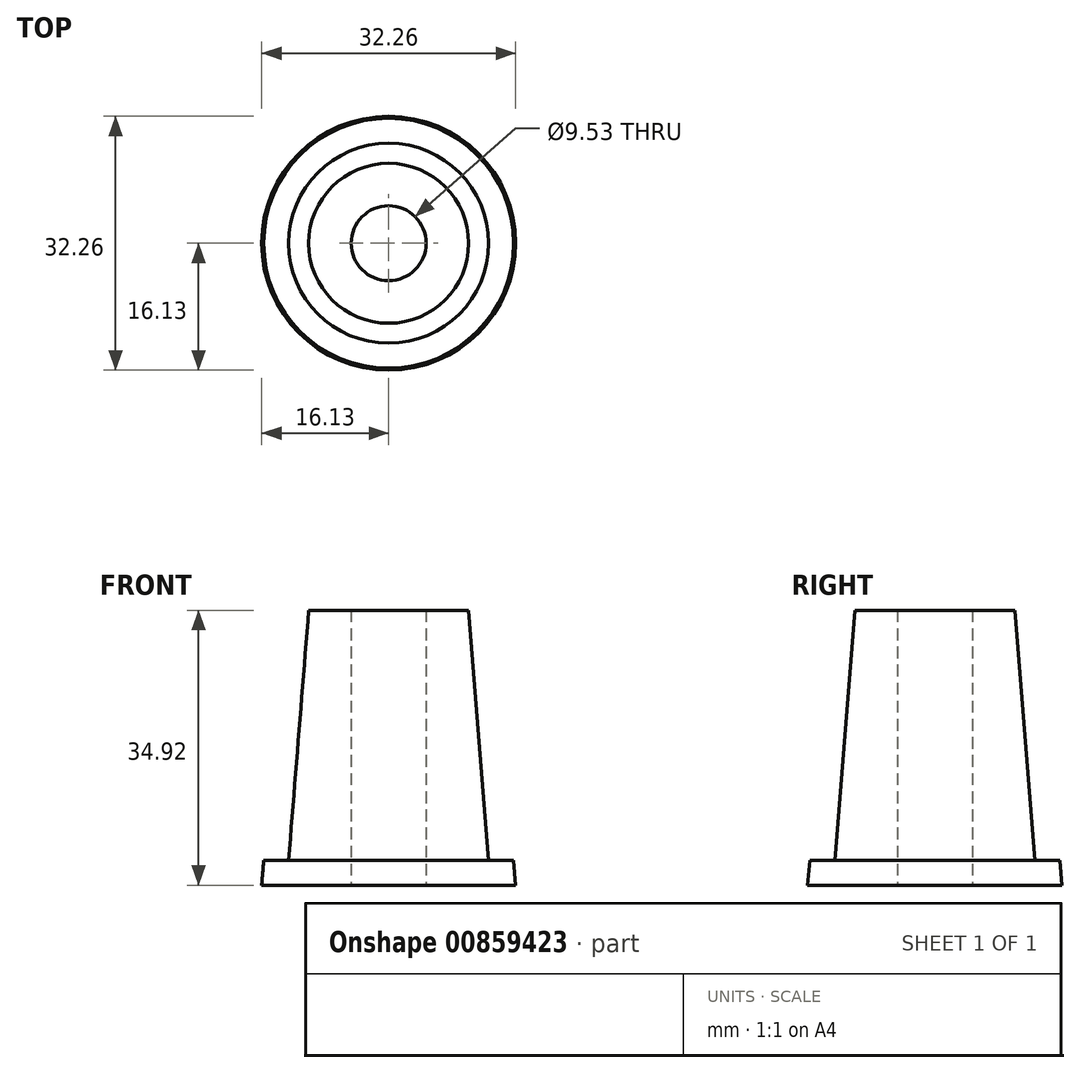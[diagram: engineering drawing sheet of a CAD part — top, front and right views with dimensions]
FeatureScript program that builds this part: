
annotation { "Feature Type Name" : "Feature", "Feature Type Description" : "" }
export const myFeature = defineFeature(function(context is Context, id is Id, definition is map)
    precondition{}
    {
        {
            var Q0;
            Q0=qCreatedBy(makeId("Front.planeOp"),FACE);
            var sketch = newSketch(context, id + "F0", { "sketchPlane" : qUnion([Q0])});
            skLineSegment(sketch, "E0", {"start": v(0, 38.9) * mm, "end": v(-10.16, 38.9) * mm});
            skLineSegment(sketch, "E1", {"start": v(-10.16, 38.9) * mm, "end": v(-12.7, 7.14) * mm});
            skLineSegment(sketch, "E2", {"start": v(-12.7, 7.14) * mm, "end": v(-15.88, 7.14) * mm});
            skLineSegment(sketch, "E3", {"start": v(-15.88, 7.14) * mm, "end": v(-16.13, 3.97) * mm});
            skLineSegment(sketch, "E4", {"start": v(-16.13, 3.97) * mm, "end": v(0, 3.97) * mm});
            skLineSegment(sketch, "E5", {"start": v(0, 3.97) * mm, "end": v(0, 38.9) * mm});
            skLineSegment(sketch, "E6", {"start": v(-4.76, 38.9) * mm, "end": v(-4.76, 3.97) * mm});
            skSolve(sketch);
        }
        {
            var Q0;
            {var subQ1=sQuery(id+"F0.wireOp",EDGE,"E1");Q0=makeQuery(id+"F0.imprint","IMPRINT",FACE,{"disambiguationData":[TD([[makeQuery(id+"F0.imprint","IMPRINT",EDGE,{"derivedFrom":subQ1}),1.0]])]});}
            var Q1;
            Q1=sQuery(id+"F0.wireOp",EDGE,"E5");
            revolve(context, id + "F1", {"surfaceOperationType" : NewSurfaceOperationType.NEW, "entities" : qUnion([Q0]), "axis" : qUnion([Q1]), "revolveType" : RevolveType.FULL});
        }
    });
